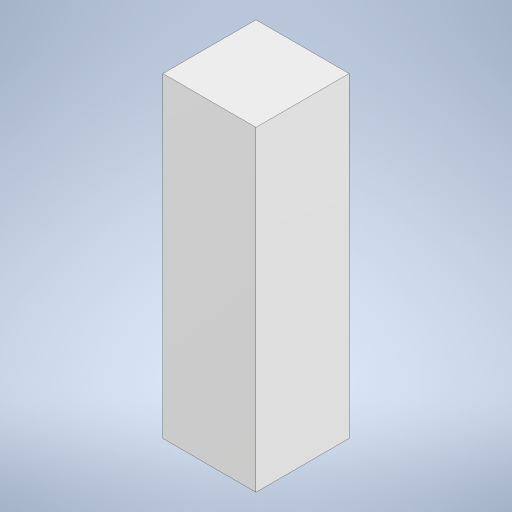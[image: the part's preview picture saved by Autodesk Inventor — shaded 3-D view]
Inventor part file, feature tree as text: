
AUTODESK INVENTOR PART (.ipt)
format: ipt  version: 2024 (Build 280153000, 153)  size: 243,200 bytes
history: native  units: in
note: dims shown in document units (in); Inventor stores cm internally (conversion verified against a paired STEP export)
features: extrude x1, sketch x1
ambient origin geometry x8: Origin, YZ Plane, XZ Plane, XY Plane, X Axis, Y Axis, Z Axis, Center Point
bodies: Solid1 (feature_tree)
feature tree (2):
  extrude  "Extrusion1"  Depth=23.0in
  sketch  "Sketch1"  dims[d1=23.0in d3=23.0in d4=78.0in d5=0.0in]
